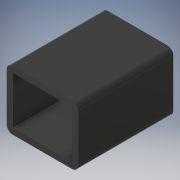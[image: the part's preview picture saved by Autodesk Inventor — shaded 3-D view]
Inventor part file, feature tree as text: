
AUTODESK INVENTOR PART (.ipt)
format: ipt  version: 2019.4 (Build 234330000, 330)  size: 122,880 bytes
history: native  units: mm
features: extrude x2, sketch x1, hole x1, fillet x1
ambient origin geometry x8: Origin, YZ Plane, XZ Plane, XY Plane, X Axis, Y Axis, Z Axis, Center Point
bodies: Solid1 (feature_tree)
feature tree (5):
  sketch  "Sketch1"  dims[d0=20.0mm d1=20.0mm d2=20.0mm d3=15.0mm d4=25.0mm d5=20.0mm d6=30.0mm d7=25.0mm d8=7.5mm d9=0.0mm d10=40.0mm d11=0.0mm d12=2.5mm d13=6.0mm d14=4.0mm d15=2.0mm d16=90.0deg d17=8.0mm d18=20.594885mm d19=2.5mm]
  extrude  "Extrusion1"  Depth=20.0mm
  extrude  "Extrusion2"  Depth=20.0mm
  hole  "Hole1"  [1 undecoded]
  fillet  "Fillet1"  Radius=25.0mm
note: 1 required parameter value undecoded (feature->parameter linkage not recoverable at this tier; creation-order binding heuristic only, values carry confidence <= 0.55)
